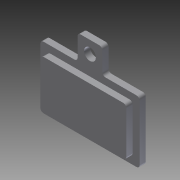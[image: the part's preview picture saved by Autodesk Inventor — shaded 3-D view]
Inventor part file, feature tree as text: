
AUTODESK INVENTOR PART (.ipt)
format: ipt  version: 2011 (Build 150239000, 239)  size: 120,320 bytes
history: native  units: in
note: dims shown in document units (in); Inventor stores cm internally (conversion verified against a paired STEP export)
features: sketch x4, extrude x3, hole x1, fillet x1
ambient origin geometry x8: Origin, YZ Plane, XZ Plane, XY Plane, X Axis, Y Axis, Z Axis, Center Point
bodies: Solid1 (feature_tree)
feature tree (9):
  extrude  "Extrusion1"  Depth=0.3937in
  extrude  "Extrusion2"  Depth=0.044in
  extrude  "Extrusion3"  Depth=0.1575in
  hole  "Hole1"  [1 undecoded]
  fillet  "Fillet1"  Radius=0.0197in
  sketch  "Sketch1"  dims[d0=0.6299in d1=0.3937in]
  sketch  "Sketch2"  dims[d2=0.0787in d3=0.0in d4=0.044in]
  sketch  "Sketch3"  dims[d5=0.0394in d6=0.0in d7=0.1575in]
  sketch  "Sketch4"  dims[d8=0.2362in d9=0.1575in d10=0.0in d11=0.075in d12=0.75in d13=0.375in d14=0.25in d15=0.5635in d16=1.0in d17=0.8108in d18=0.0197in]
note: 1 required parameter value undecoded (feature->parameter linkage not recoverable at this tier; creation-order binding heuristic only, values carry confidence <= 0.55)
